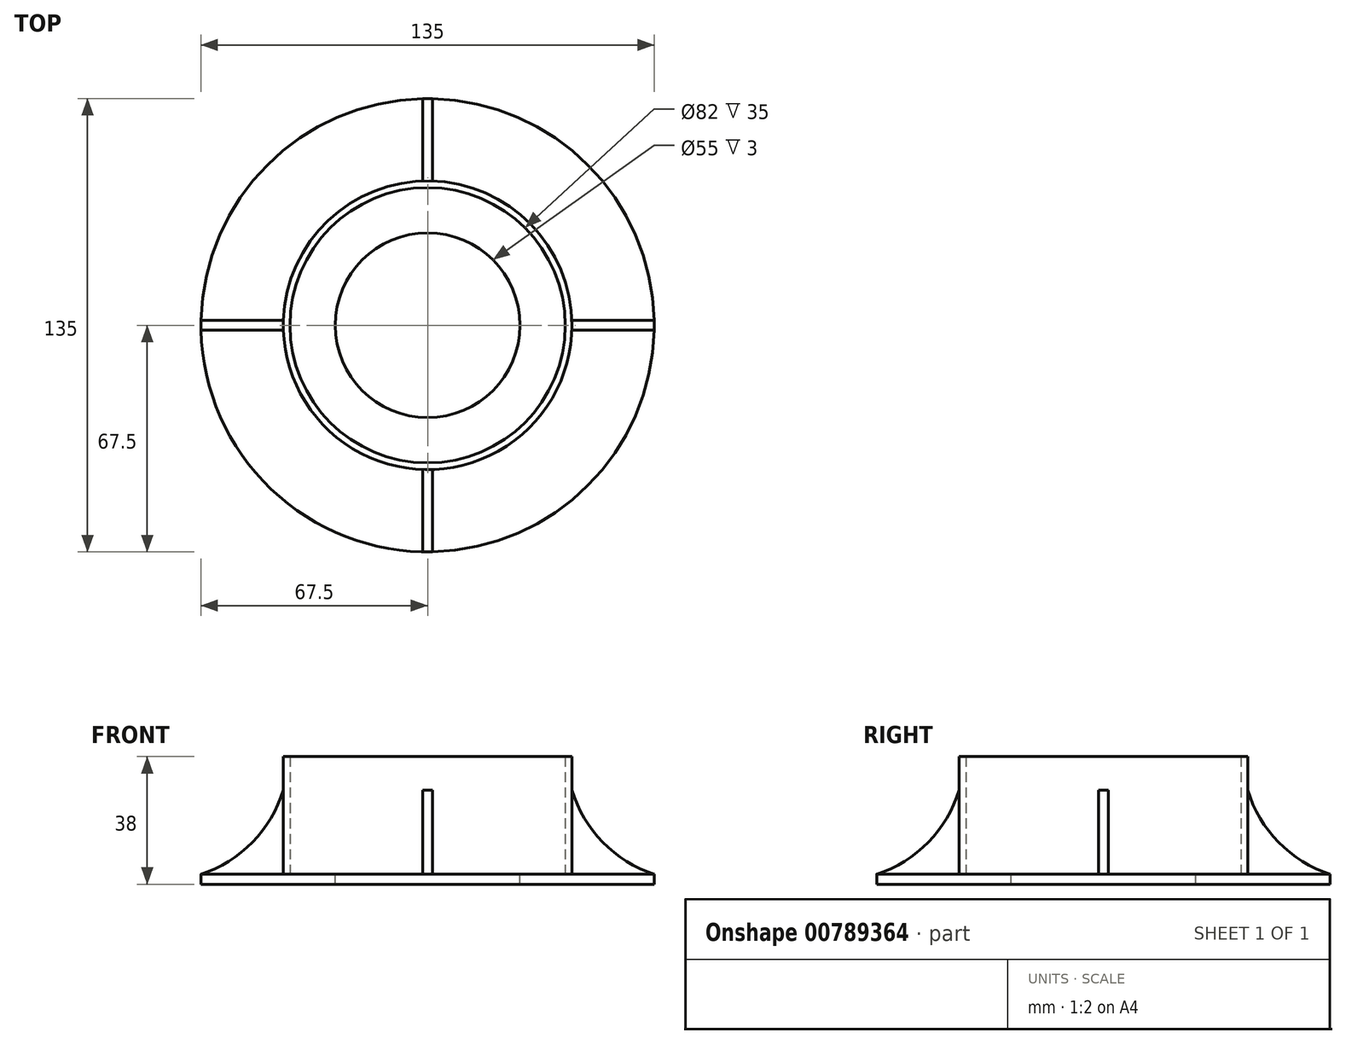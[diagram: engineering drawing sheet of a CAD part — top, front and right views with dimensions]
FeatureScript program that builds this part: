
annotation { "Feature Type Name" : "Feature", "Feature Type Description" : "" }
export const myFeature = defineFeature(function(context is Context, id is Id, definition is map)
    precondition{}
    {
        {
            var Q0;
            Q0=qCreatedBy(makeId("Top.planeOp"),FACE);
            var sketch = newSketch(context, id + "F0", { "sketchPlane" : qUnion([Q0])});
            skCircle(sketch, "E0", {"center": v(0, 0) * mm, "radius": 67.5 * mm});
            skSolve(sketch);
        }
        {
            var Q0;
            Q0=makeQuery(id+"F0.imprint","IMPRINT",FACE,{"disambiguationData":[TD([[makeQuery(id+"F0.imprint","IMPRINT",EDGE,{"derivedFrom":sQuery(id+"F0.wireOp",EDGE,"E0")}),1.0]])]});
            extrude(context, id + "F1", {"entities" : qUnion([Q0]), "depth" : 3 * mm, "offsetDistance" : 25 * mm});
        }
        {
            var Q0;
            Q0=makeQuery(id+"F1.opExtrude","CAP_FACE",FACE,{"disambiguationData":[OSD([sQuery(id+"F0.wireOp",EDGE,"E0")])],"isStart":false});
            var sketch = newSketch(context, id + "F2", { "sketchPlane" : qUnion([Q0])});
            skCircle(sketch, "E1", {"center": v(0, 0) * mm, "radius": 41 * mm});
            skCircle(sketch, "E2", {"center": v(0, 0) * mm, "radius": 43 * mm});
            skSolve(sketch);
        }
        {
            var Q0;
            Q0=makeQuery(id+"F2.imprint","IMPRINT",FACE,{"disambiguationData":[TD([[makeQuery(id+"F2.imprint","IMPRINT",EDGE,{"derivedFrom":sQuery(id+"F2.wireOp",EDGE,"E1")}),-1.0]])]});
            extrude(context, id + "F3", {"entities" : qUnion([Q0]), "operationType" : NewBodyOperationType.ADD, "depth" : 35 * mm, "offsetDistance" : 25 * mm});
        }
        {
            var Q0;
            Q0=makeQuery(id+"F3.boolean.opBoolean","SPLIT",FACE,{"disambiguationData":[TD([makeQuery(id+"F3.opExtrude","SWEPT_FACE",FACE,{"disambiguationData":[OSD([sQuery(id+"F2.wireOp",EDGE,"E1")])]})])],"derivedFrom":makeQuery(id+"F1.opExtrude","CAP_FACE",FACE,{"disambiguationData":[OSD([sQuery(id+"F0.wireOp",EDGE,"E0")])],"isStart":false})});
            var sketch = newSketch(context, id + "F4", { "sketchPlane" : qUnion([Q0])});
            skCircle(sketch, "E3", {"center": v(0, 0) * mm, "radius": 27.5 * mm});
            skSolve(sketch);
        }
        {
            var Q0;
            Q0=makeQuery(id+"F4.imprint","IMPRINT",FACE,{"disambiguationData":[TD([[makeQuery(id+"F4.imprint","IMPRINT",EDGE,{"derivedFrom":sQuery(id+"F4.wireOp",EDGE,"E3")}),1.0]])]});
            extrude(context, id + "F5", {"entities" : qUnion([Q0]), "operationType" : NewBodyOperationType.REMOVE, "oppositeDirection" : true, "depth" : 3 * mm, "offsetDistance" : 25 * mm});
        }
        {
            var Q0;
            {var subQ0=sQuery(id+"F0.wireOp",EDGE,"E0");Q0=makeQuery(id+"F3.boolean.opBoolean","SPLIT",FACE,{"disambiguationData":[TD([makeQuery(id+"F1.opExtrude","SWEPT_FACE",FACE,{"disambiguationData":[OSD([subQ0])]})])],"derivedFrom":makeQuery(id+"F1.opExtrude","CAP_FACE",FACE,{"disambiguationData":[OSD([subQ0])],"isStart":false})});}
            var sketch = newSketch(context, id + "F6", { "sketchPlane" : qUnion([Q0])});
            skLineSegment(sketch, "E4.bottom", {"start": v(1.5, 67.5) * mm, "end": v(-1.5, 67.5) * mm});
            skLineSegment(sketch, "E4.top", {"start": v(1.5, 41.5) * mm, "end": v(-1.5, 41.5) * mm});
            skLineSegment(sketch, "E4.left", {"start": v(1.5, 67.5) * mm, "end": v(1.5, 41.5) * mm});
            skLineSegment(sketch, "E4.right", {"start": v(-1.5, 67.5) * mm, "end": v(-1.5, 41.5) * mm});
            skLineSegment(sketch, "E5.bottom", {"start": v(67.48, 1.5) * mm, "end": v(41.48, 1.5) * mm});
            skLineSegment(sketch, "E5.top", {"start": v(67.48, -1.5) * mm, "end": v(41.48, -1.5) * mm});
            skLineSegment(sketch, "E5.left", {"start": v(67.48, 1.5) * mm, "end": v(67.48, -1.5) * mm});
            skLineSegment(sketch, "E5.right", {"start": v(41.48, 1.5) * mm, "end": v(41.48, -1.5) * mm});
            skLineSegment(sketch, "E6.bottom", {"start": v(-67.48, 1.5) * mm, "end": v(-41.48, 1.5) * mm});
            skLineSegment(sketch, "E6.top", {"start": v(-67.48, -1.5) * mm, "end": v(-41.48, -1.5) * mm});
            skLineSegment(sketch, "E6.left", {"start": v(-67.48, 1.5) * mm, "end": v(-67.48, -1.5) * mm});
            skLineSegment(sketch, "E6.right", {"start": v(-41.48, 1.5) * mm, "end": v(-41.48, -1.5) * mm});
            skLineSegment(sketch, "E7.bottom", {"start": v(1.51, -41.97) * mm, "end": v(-1.49, -41.97) * mm});
            skLineSegment(sketch, "E7.top", {"start": v(1.51, -67.97) * mm, "end": v(-1.49, -67.97) * mm});
            skLineSegment(sketch, "E7.left", {"start": v(1.51, -41.97) * mm, "end": v(1.51, -67.97) * mm});
            skLineSegment(sketch, "E7.right", {"start": v(-1.49, -41.97) * mm, "end": v(-1.49, -67.97) * mm});
            skSolve(sketch);
        }
        {
            var Q0;
            {var subQ3=makeQuery(id+"F1.opExtrude","CAP_EDGE",EDGE,{"disambiguationData":[OSD([sQuery(id+"F0.wireOp",EDGE,"E0")])],"isStart":false});var subQ5=sQuery(id+"F6.wireOp",EDGE,"E7.right");var subQ7=makeQuery(id+"F6.imprint","INTERSECT",VERTEX,{"derivedFrom":[subQ3,subQ5]});Q0=makeQuery(id+"F6.imprint","IMPRINT",FACE,{"disambiguationData":[TD([[makeQuery(id+"F6.imprint","IMPRINT",EDGE,{"disambiguationData":[TD([[subQ7,1.0]])],"derivedFrom":subQ5}),1.0]])]});}
            var Q1;
            {var subQ0=sQuery(id+"F6.wireOp",EDGE,"E5.left");Q1=makeQuery(id+"F6.imprint","IMPRINT",FACE,{"disambiguationData":[TD([[makeQuery(id+"F6.imprint","IMPRINT",EDGE,{"derivedFrom":subQ0}),-1.0]])]});}
            var Q2;
            {var subQ0=sQuery(id+"F6.wireOp",EDGE,"E6.left");Q2=makeQuery(id+"F6.imprint","IMPRINT",FACE,{"disambiguationData":[TD([[makeQuery(id+"F6.imprint","IMPRINT",EDGE,{"derivedFrom":subQ0}),1.0]])]});}
            var Q3;
            {var subQ0=makeQuery(id+"F1.opExtrude","CAP_EDGE",EDGE,{"disambiguationData":[OSD([sQuery(id+"F0.wireOp",EDGE,"E0")])],"isStart":false});var subQ6=sQuery(id+"F6.wireOp",EDGE,"E4.left");var subQ7=makeQuery(id+"F6.imprint","INTERSECT",VERTEX,{"derivedFrom":[subQ0,subQ6]});Q3=makeQuery(id+"F6.imprint","IMPRINT",FACE,{"disambiguationData":[TD([[makeQuery(id+"F6.imprint","IMPRINT",EDGE,{"disambiguationData":[TD([[subQ7,-1.0]])],"derivedFrom":subQ6}),-1.0]])]});}
            extrude(context, id + "F7", {"entities" : qUnion([Q0, Q1, Q2, Q3]), "operationType" : NewBodyOperationType.ADD, "depth" : 25 * mm, "offsetDistance" : 25 * mm});
        }
        {
            var Q0;
            Q0=makeQuery(id+"F7.opExtrude","SWEPT_FACE",FACE,{"disambiguationData":[OSD([sQuery(id+"F6.wireOp",EDGE,"E5.bottom")])]});
            var sketch = newSketch(context, id + "F8", { "sketchPlane" : qUnion([Q0])});
            skArc(sketch, "E8", {"start": v(-67.48, 3) * mm, "mid": v(-52.18, 12.5) * mm, "end": v(-42.97, 28) * mm});
            skSolve(sketch);
        }
        {
            var Q0;
            Q0=makeQuery(id+"F7.opExtrude","SWEPT_FACE",FACE,{"disambiguationData":[OSD([sQuery(id+"F6.wireOp",EDGE,"E4.right")])]});
            var sketch = newSketch(context, id + "F9", { "sketchPlane" : qUnion([Q0])});
            skArc(sketch, "E9", {"start": v(-67.48, 3) * mm, "mid": v(-52.18, 12.5) * mm, "end": v(-42.97, 28) * mm});
            skSolve(sketch);
        }
        {
            var Q0;
            Q0=makeQuery(id+"F7.opExtrude","SWEPT_FACE",FACE,{"disambiguationData":[OSD([sQuery(id+"F6.wireOp",EDGE,"E6.top")])]});
            var sketch = newSketch(context, id + "F10", { "sketchPlane" : qUnion([Q0])});
            skArc(sketch, "E10", {"start": v(-67.48, 3) * mm, "mid": v(-52.18, 12.5) * mm, "end": v(-42.97, 28) * mm});
            skSolve(sketch);
        }
        {
            var Q0;
            Q0=makeQuery(id+"F7.opExtrude","SWEPT_FACE",FACE,{"disambiguationData":[OSD([sQuery(id+"F6.wireOp",EDGE,"E7.left")])]});
            var sketch = newSketch(context, id + "F11", { "sketchPlane" : qUnion([Q0])});
            skArc(sketch, "E11", {"start": v(-67.48, 3) * mm, "mid": v(-52.18, 12.5) * mm, "end": v(-42.97, 28) * mm});
            skSolve(sketch);
        }
        {
            var Q0;
            Q0=makeQuery(id+"F11.imprint","IMPRINT",FACE,{"disambiguationData":[TD([[makeQuery(id+"F11.imprint","IMPRINT",EDGE,{"derivedFrom":sQuery(id+"F11.wireOp",EDGE,"E11")}),1.0]])]});
            extrude(context, id + "F12", {"entities" : qUnion([Q0]), "operationType" : NewBodyOperationType.REMOVE, "oppositeDirection" : true, "depth" : 25 * mm, "offsetDistance" : 25 * mm});
        }
        {
            var Q0;
            Q0=makeQuery(id+"F8.imprint","IMPRINT",FACE,{"disambiguationData":[TD([[makeQuery(id+"F8.imprint","IMPRINT",EDGE,{"derivedFrom":sQuery(id+"F8.wireOp",EDGE,"E8")}),1.0]])]});
            extrude(context, id + "F13", {"entities" : qUnion([Q0]), "operationType" : NewBodyOperationType.REMOVE, "oppositeDirection" : true, "depth" : 25 * mm, "offsetDistance" : 25 * mm});
        }
        {
            var Q0;
            Q0=makeQuery(id+"F9.imprint","IMPRINT",FACE,{"disambiguationData":[TD([[makeQuery(id+"F9.imprint","IMPRINT",EDGE,{"derivedFrom":sQuery(id+"F9.wireOp",EDGE,"E9")}),1.0]])]});
            extrude(context, id + "F14", {"entities" : qUnion([Q0]), "operationType" : NewBodyOperationType.REMOVE, "surfaceOperationType" : NewSurfaceOperationType.ADD, "oppositeDirection" : true, "depth" : 25 * mm, "offsetDistance" : 25 * mm});
        }
        {
            var Q0;
            Q0=makeQuery(id+"F10.imprint","IMPRINT",FACE,{"disambiguationData":[TD([[makeQuery(id+"F10.imprint","IMPRINT",EDGE,{"derivedFrom":sQuery(id+"F10.wireOp",EDGE,"E10")}),1.0]])]});
            extrude(context, id + "F15", {"entities" : qUnion([Q0]), "operationType" : NewBodyOperationType.REMOVE, "oppositeDirection" : true, "depth" : 25 * mm, "offsetDistance" : 25 * mm});
        }
        {
            var Q0;
            Q0=makeQuery(id+"F7.opExtrude","CAP_FACE",FACE,{"disambiguationData":[OSD([sQuery(id+"F0.wireOp",EDGE,"E0"),sQuery(id+"F2.wireOp",EDGE,"E2"),sQuery(id+"F6.wireOp",EDGE,"E7.left"),sQuery(id+"F6.wireOp",EDGE,"E7.right")])],"isStart":false});
            var Q1;
            Q1=makeQuery(id+"F7.opExtrude","CAP_FACE",FACE,{"disambiguationData":[OSD([sQuery(id+"F0.wireOp",EDGE,"E0"),sQuery(id+"F2.wireOp",EDGE,"E2"),sQuery(id+"F6.wireOp",EDGE,"E4.left"),sQuery(id+"F6.wireOp",EDGE,"E4.right")])],"isStart":false});
            var Q2;
            {var subQ0=makeQuery(id+"F3.opExtrude","SWEPT_FACE",FACE,{"disambiguationData":[OSD([sQuery(id+"F2.wireOp",EDGE,"E2")])]});var subQ1=sQuery(id+"F0.wireOp",EDGE,"E0");var subQ2=makeQuery(id+"F1.opExtrude","CAP_FACE",FACE,{"disambiguationData":[OSD([subQ1])],"isStart":false});var subQ3=makeQuery(id+"F1.opExtrude","SWEPT_FACE",FACE,{"disambiguationData":[OSD([subQ1])]});var subQ4=sQuery(id+"F6.wireOp",EDGE,"E7.right");var subQ5=makeQuery(id+"F1.opExtrude","CAP_EDGE",EDGE,{"disambiguationData":[OSD([subQ1])],"isStart":false});var subQ6=makeQuery(id+"F6.imprint","INTERSECT",VERTEX,{"derivedFrom":[subQ5,sQuery(id+"F6.wireOp",EDGE,"E4.bottom")]});Q2=makeQuery(id+"F7.boolean.opBoolean","SPLIT",FACE,{"disambiguationData":[TD([subQ3,subQ2,subQ0,makeQuery(id+"F7.opExtrude","SWEPT_FACE",FACE,{"disambiguationData":[OSD([sQuery(id+"F6.wireOp",EDGE,"E6.top")])]}),makeQuery(id+"F7.opExtrude","SWEPT_FACE",FACE,{"disambiguationData":[OSD([sQuery(id+"F6.wireOp",EDGE,"E6.left")])]}),makeQuery(id+"F7.opExtrude","SWEPT_FACE",FACE,{"disambiguationData":[OSD([subQ4])]}),makeQuery(id+"F7.opExtrude","SWEPT_FACE",FACE,{"disambiguationData":[OSD([subQ1]),TDD([makeQuery(id+"F6.imprint","IMPRINT",EDGE,{"disambiguationData":[TD([[subQ6,1.0]])],"derivedFrom":subQ5}),makeQuery(id+"F6.imprint","IMPRINT",EDGE,{"disambiguationData":[TD([[subQ6,-1.0]])],"derivedFrom":subQ5})])]}),makeQuery(id+"F7.opExtrude","SWEPT_FACE",FACE,{"disambiguationData":[OSD([subQ1]),TDD([makeQuery(id+"F6.imprint","IMPRINT",EDGE,{"disambiguationData":[TD([[makeQuery(id+"F6.imprint","INTERSECT",VERTEX,{"derivedFrom":[subQ5,sQuery(id+"F6.wireOp",EDGE,"E7.left")]}),1.0]])],"derivedFrom":subQ5})])]})])],"derivedFrom":makeQuery(id+"F3.boolean.opBoolean","SPLIT",FACE,{"disambiguationData":[TD([subQ3])],"derivedFrom":subQ2})});}
            extrude(context, id + "F16", {"entities" : qUnion([Q0, Q1]), "operationType" : NewBodyOperationType.REMOVE, "endBound" : BoundingType.UP_TO_SURFACE, "oppositeDirection" : true, "depth" : 25 * mm, "endBoundEntityFace" : qUnion([Q2]), "offsetDistance" : 25 * mm});
        }
    });
